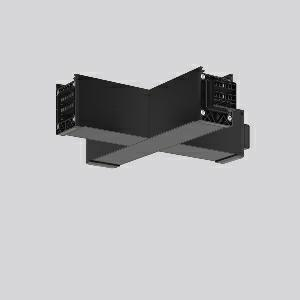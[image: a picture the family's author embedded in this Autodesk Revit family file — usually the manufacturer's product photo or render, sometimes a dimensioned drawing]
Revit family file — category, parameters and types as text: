
# Revit family: linedo_x-verbindung_982775_003_6ed3
name_source: partatom
category: Lighting Fixtures
units: mm (PartAtom-declared; Revit-internal decimal feet)

## family parameters
Cut with Voids When Loaded = No
Host = Face
Light Source = No
Part Type = Normal
Room Calculation Point = No
Round Connector Dimension = Use Diameter
Shared = No

## types (1)
- LINEDO X-Verbindung
    Apparent Load = 0 VA
    Default Elevation = 1800 mm
    Description = Series: LINEDO
X-connector, 14-pole, connection plug / socket / plug / socket. Housing: extruded aluminium profile, powder-coated. Cover made of plastic, surface like housing. LINEDO plug system, plastic, black. Easy connection for rigid or flexible wires. 6 membrane cable entries (2 x M20 and 4 x M25). Suitable for power supply in 7-pole version. Ready prewired. Colour-coded individual cables enable easy electromechanical separation.
Colour: jet black (RAL 9005)
Length: 330 mm
Width: 330 mm
Height: 76 mm
Weight: 1410 g
    Height = 76 mm
    Lamp = 0 x
    Length = 331 mm
    Luminous efficacy = 0 lm/W
    Manufacturer = RZB
    ModVariant = No
    Model = 982775.003
    Mounting Place = Ceiling
    Mounting Type = Surface mounted
    Number of Poles = 1
    OnlyDefault = Yes
    Power Factor = 1
    Product Name = LINEDO X-Verbindung
    Product group = Continuous line luminaire system Linedo IP 54
    ProductGroupID = 314
    Protection Class = Protection class I
    Protection Degree = Degree of protection
    RLX_Detail_Level = 1
    RLX_Emergency_Light_Flux = 0 lm
    RLX_Emergency_Type = 0
    RLX_Emergency_Type_DB = No
    RlxData = <blob elided: 22777 chars, md5=4202e20c>
    Standby Power = 0 W
    System Light Flux = 0 lm
    System Power = 0 W
    Type Comments = Product without accessories
    Type Image = 982775.003.jpg
    URL = http://relux.com
    VarID = ---
    Voltage = 0 V
    Weight = 0.00 kg
    Width = 331 mm

## geometry (parser evidence)
native form markers: Blend x4, Sweep x12
no freeform markers — native parametric forms only
